# Revit family: Haworth_Openest_DoubleDesk
name_source: partatom
category: Furniture
revit_build: Autodesk Revit 2018 (Build: 20170223_1515(x64)
units: mm (PartAtom-declared; Revit-internal decimal feet)

## family parameters
Always vertical = Yes
Cut with Voids When Loaded = No
OmniClass Number = 23.40.20.00
OmniClass Title = General Furniture and Specialties
Room Calculation Point = No
Shared = No
Work Plane-Based = No

## types (1)
- Double Desk
    Actual Coat Hook = Yes
    Actual Depth = 9' - 9"
    Actual Width = 2' - 5"
    Assembly Code = E2020200
    Coat Hook = Yes
    Description = Haworth - Openest - Double Desk
    Manufacturer = Haworth
    Model = HOAD
    Monitor Mount = No
    Reference Info = Coat Hook Not Available w/ Monitor Mount
    Revision No. = 2
    Soft Storage = Yes
    Sustainability Info = https://www.haworth.com
    URL = http://www.haworth.com
    URL - Product = https://www.haworth.com
    Warranty = http://www.haworth.com

## geometry (parser evidence)
native form markers: Sweep x22
no freeform markers — native parametric forms only
